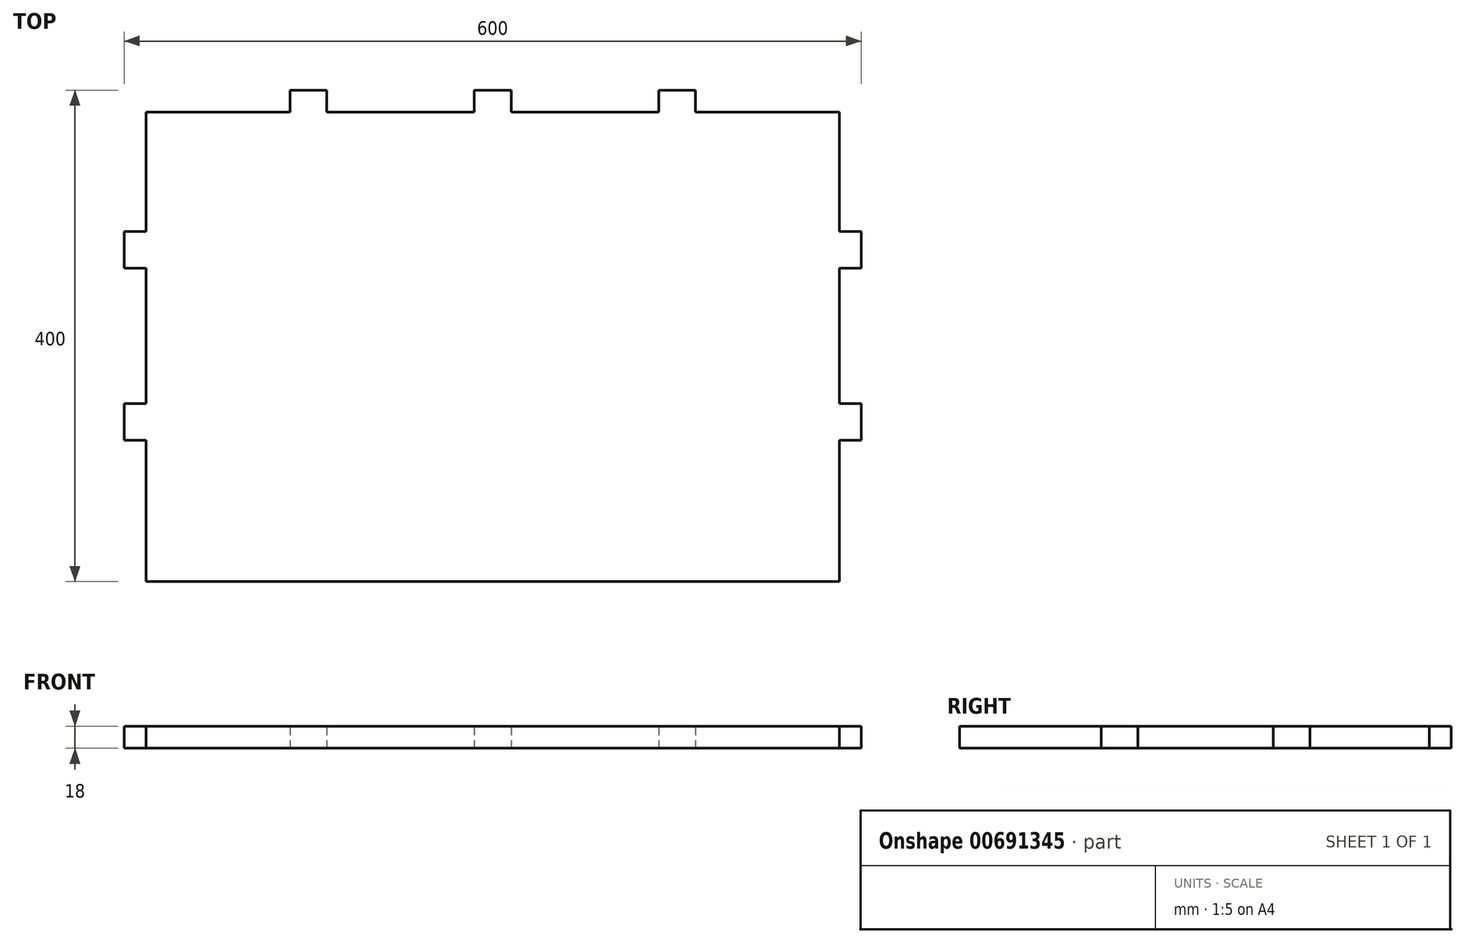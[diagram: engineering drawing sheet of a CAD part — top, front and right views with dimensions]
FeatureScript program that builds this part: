
annotation { "Feature Type Name" : "Feature", "Feature Type Description" : "" }
export const myFeature = defineFeature(function(context is Context, id is Id, definition is map)
    precondition{}
    {
        {
            var Q0;
            Q0=qCreatedBy(makeId("Right.planeOp"),FACE);
            var sketch = newSketch(context, id + "F0", { "sketchPlane" : qUnion([Q0])});
            skLineSegment(sketch, "E0", {"start": v(0, 0) * mm, "end": v(0, 18) * mm});
            skLineSegment(sketch, "E1", {"start": v(0, 18) * mm, "end": v(400, 18) * mm});
            skLineSegment(sketch, "E2", {"start": v(400, 18) * mm, "end": v(400, 0) * mm});
            skLineSegment(sketch, "E3", {"start": v(400, 0) * mm, "end": v(0, 0) * mm});
            skSolve(sketch);
        }
        {
            var Q0;
            Q0=qCreatedBy(makeId("Top.planeOp"),FACE);
            var sketch = newSketch(context, id + "F1", { "sketchPlane" : qUnion([Q0])});
            skLineSegment(sketch, "E4", {"start": v(-300, -47.28) * mm, "end": v(-300, 479.56) * mm, "construction": true});
            skLineSegment(sketch, "E5", {"start": v(-652.6, 200) * mm, "end": v(61.07, 200) * mm, "construction": true});
            skLineSegment(sketch, "E6.MirrorCS", {"start": v(-582, 145) * mm, "end": v(-582, 130) * mm, "construction": true});
            skLineSegment(sketch, "E7.MirrorCS", {"start": v(-582, 115) * mm, "end": v(-582, 130) * mm, "construction": true});
            skLineSegment(sketch, "E8.MirrorCS", {"start": v(0, 270) * mm, "end": v(-18, 270) * mm, "construction": true});
            skLineSegment(sketch, "E9.MirrorCS", {"start": v(-18, 145) * mm, "end": v(-18, 130) * mm, "construction": true});
            skLineSegment(sketch, "E10.MirrorCS", {"start": v(-18, 115) * mm, "end": v(-18, 130) * mm, "construction": true});
            skPoint(sketch, "E11.orphan", {"position": v(0, 200) * mm});
            skPoint(sketch, "E12.orphan", {"position": v(-600, 200) * mm});
            skLineSegment(sketch, "E13", {"start": v(-582, 145) * mm, "end": v(-582, 255) * mm});
            skLineSegment(sketch, "E14", {"start": v(-582, 285) * mm, "end": v(-582, 382) * mm});
            skLineSegment(sketch, "E15", {"start": v(-582, 115) * mm, "end": v(-582, 0) * mm});
            skLineSegment(sketch, "E16", {"start": v(-465, 382) * mm, "end": v(-582, 382) * mm});
            skLineSegment(sketch, "E17", {"start": v(-435, 382) * mm, "end": v(-315, 382) * mm});
            skLineSegment(sketch, "E18", {"start": v(-285, 382) * mm, "end": v(-165, 382) * mm});
            skLineSegment(sketch, "E19", {"start": v(-18, 285) * mm, "end": v(-18, 382) * mm});
            skLineSegment(sketch, "E20", {"start": v(-18, 382) * mm, "end": v(-135, 382) * mm});
            skLineSegment(sketch, "E21", {"start": v(-18, 255) * mm, "end": v(-18, 145) * mm});
            skLineSegment(sketch, "E22", {"start": v(-18, 115) * mm, "end": v(-18, 0) * mm});
            skLineSegment(sketch, "E23", {"start": v(-582, 0) * mm, "end": v(-18, 0) * mm});
            skLineSegment(sketch, "E24", {"start": v(-582, 115) * mm, "end": v(-600, 115) * mm});
            skLineSegment(sketch, "E25", {"start": v(-582, 145) * mm, "end": v(-600, 145) * mm});
            skLineSegment(sketch, "E26", {"start": v(-582, 255) * mm, "end": v(-600, 255) * mm});
            skLineSegment(sketch, "E27", {"start": v(-582, 285) * mm, "end": v(-600, 285) * mm});
            skLineSegment(sketch, "E28", {"start": v(-465, 382) * mm, "end": v(-465, 400) * mm});
            skLineSegment(sketch, "E29", {"start": v(-435, 382) * mm, "end": v(-435, 400) * mm});
            skLineSegment(sketch, "E30", {"start": v(-315, 382) * mm, "end": v(-315, 400) * mm});
            skLineSegment(sketch, "E31", {"start": v(-285, 382) * mm, "end": v(-285, 400) * mm});
            skLineSegment(sketch, "E32", {"start": v(-165, 382) * mm, "end": v(-165, 400) * mm});
            skLineSegment(sketch, "E33", {"start": v(-135, 382) * mm, "end": v(-135, 400) * mm});
            skLineSegment(sketch, "E34", {"start": v(-18, 285) * mm, "end": v(0, 285) * mm});
            skLineSegment(sketch, "E35", {"start": v(-18, 255) * mm, "end": v(0, 255) * mm});
            skLineSegment(sketch, "E36", {"start": v(-18, 145) * mm, "end": v(0, 145) * mm});
            skLineSegment(sketch, "E37", {"start": v(-18, 115) * mm, "end": v(0, 115) * mm});
            skLineSegment(sketch, "E38", {"start": v(-135, 400) * mm, "end": v(-165, 400) * mm});
            skLineSegment(sketch, "E39", {"start": v(-315, 400) * mm, "end": v(-285, 400) * mm});
            skLineSegment(sketch, "E40", {"start": v(-465, 400) * mm, "end": v(-435, 400) * mm});
            skLineSegment(sketch, "E41", {"start": v(-600, 255) * mm, "end": v(-600, 285) * mm});
            skLineSegment(sketch, "E42", {"start": v(-600, 145) * mm, "end": v(-600, 115) * mm});
            skLineSegment(sketch, "E43", {"start": v(0, 145) * mm, "end": v(0, 115) * mm});
            skLineSegment(sketch, "E44", {"start": v(0, 285) * mm, "end": v(0, 255) * mm});
            skPoint(sketch, "E45.3.start.orphan", {"position": v(0, 400) * mm});
            skPoint(sketch, "E45.1.start.orphan", {"position": v(0, 0) * mm});
            skLineSegment(sketch, "E46", {"start": v(-18, 270) * mm, "end": v(-582, 270) * mm, "construction": true});
            skPoint(sketch, "E47.MirrorCS.end.orphan", {"position": v(-582, 270) * mm});
            skPoint(sketch, "E47.MirrorCS.start.orphan", {"position": v(-582, 285) * mm});
            skPoint(sketch, "E48.MirrorCS.start.orphan", {"position": v(-582, 255) * mm});
            skSolve(sketch);
        }
        {
            var Q0;
            Q0=makeQuery(id+"F1.imprint","IMPRINT",FACE,{"disambiguationData":[TD([[makeQuery(id+"F1.imprint","IMPRINT",EDGE,{"derivedFrom":sQuery(id+"F1.wireOp",EDGE,"E13")}),-1.0]])]});
            extrude(context, id + "F2", {"entities" : qUnion([Q0]), "depth" : 18 * mm, "offsetDistance" : 25 * mm});
        }
        {
            var Q0;
            Q0=makeQuery(id+"F2.opExtrude","SWEPT_BODY",BODY,{"disambiguationData":[OSD([sQuery(id+"F1.wireOp",EDGE,"E13"),sQuery(id+"F1.wireOp",EDGE,"E14"),sQuery(id+"F1.wireOp",EDGE,"E15"),sQuery(id+"F1.wireOp",EDGE,"E16"),sQuery(id+"F1.wireOp",EDGE,"E17"),sQuery(id+"F1.wireOp",EDGE,"E18"),sQuery(id+"F1.wireOp",EDGE,"E19"),sQuery(id+"F1.wireOp",EDGE,"E20"),sQuery(id+"F1.wireOp",EDGE,"E21"),sQuery(id+"F1.wireOp",EDGE,"E22"),sQuery(id+"F1.wireOp",EDGE,"E23"),sQuery(id+"F1.wireOp",EDGE,"E24"),sQuery(id+"F1.wireOp",EDGE,"E25"),sQuery(id+"F1.wireOp",EDGE,"E26"),sQuery(id+"F1.wireOp",EDGE,"E27"),sQuery(id+"F1.wireOp",EDGE,"E28"),sQuery(id+"F1.wireOp",EDGE,"E29"),sQuery(id+"F1.wireOp",EDGE,"E30"),sQuery(id+"F1.wireOp",EDGE,"E31"),sQuery(id+"F1.wireOp",EDGE,"E32"),sQuery(id+"F1.wireOp",EDGE,"E33"),sQuery(id+"F1.wireOp",EDGE,"E34"),sQuery(id+"F1.wireOp",EDGE,"E35"),sQuery(id+"F1.wireOp",EDGE,"E36"),sQuery(id+"F1.wireOp",EDGE,"E37"),sQuery(id+"F1.wireOp",EDGE,"E38"),sQuery(id+"F1.wireOp",EDGE,"E39"),sQuery(id+"F1.wireOp",EDGE,"E40"),sQuery(id+"F1.wireOp",EDGE,"E41"),sQuery(id+"F1.wireOp",EDGE,"E42"),sQuery(id+"F1.wireOp",EDGE,"E43"),sQuery(id+"F1.wireOp",EDGE,"E44")])]});
            transform(context, id + "F3", {"entities" : qUnion([Q0]), "transformType" : TransformType.TRANSLATION_3D, "dx" : 0 * mm, "dy" : 0 * mm, "dz" : 0 * mm, "makeCopy" : true});
        }
    });
